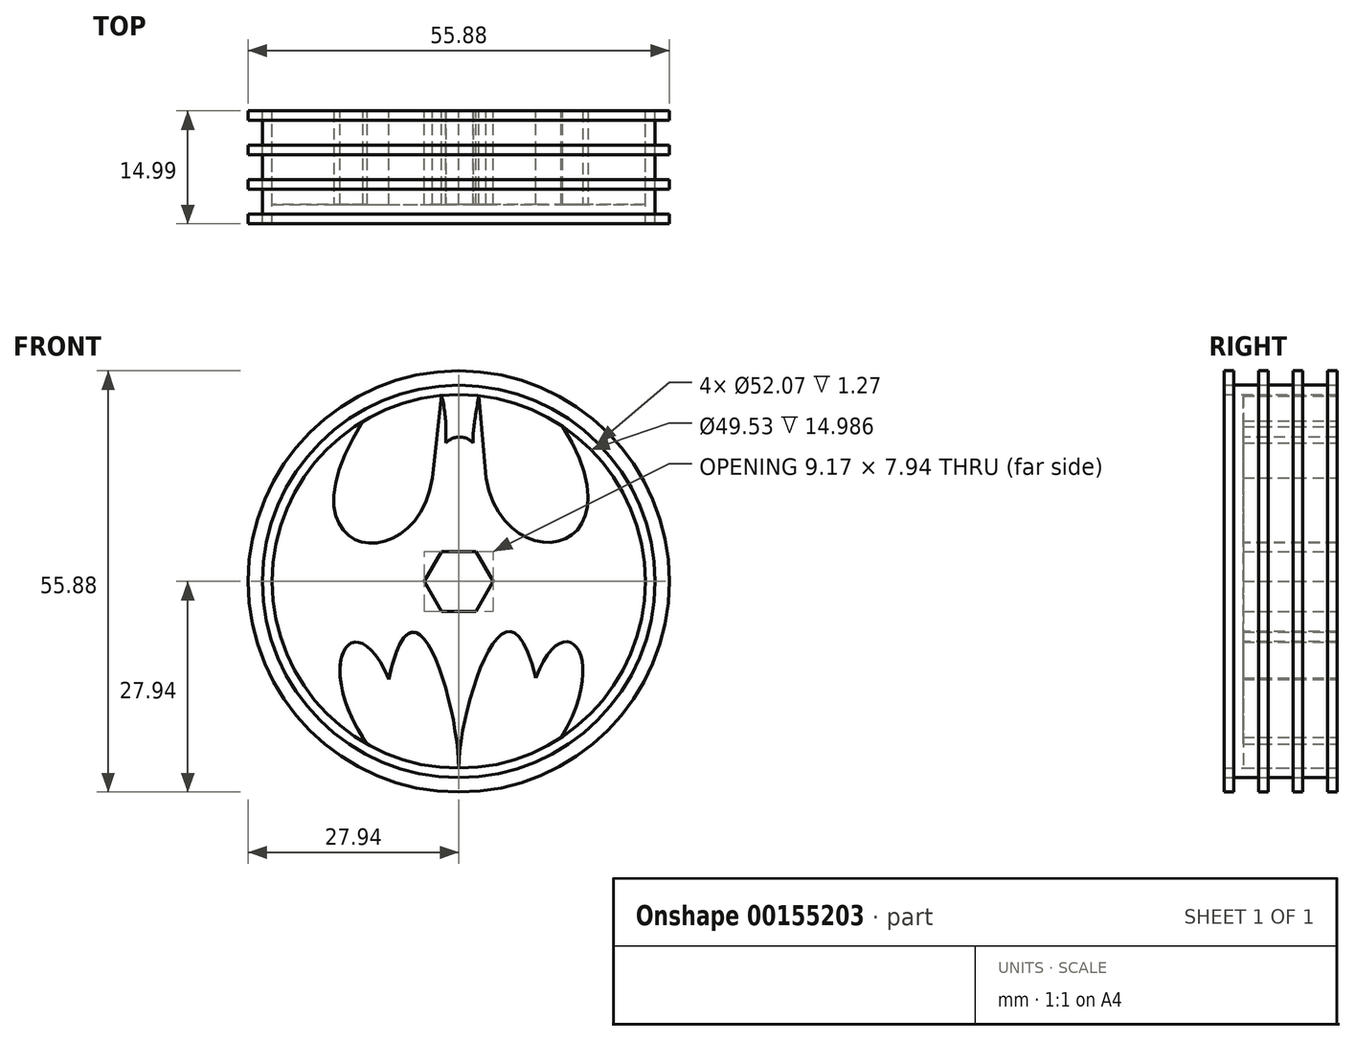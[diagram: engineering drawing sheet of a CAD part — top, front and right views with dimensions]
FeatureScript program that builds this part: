
annotation { "Feature Type Name" : "Feature", "Feature Type Description" : "" }
export const myFeature = defineFeature(function(context is Context, id is Id, definition is map)
    precondition{}
    {
        {
            var Q0;
            Q0=qCreatedBy(makeId("Front.planeOp"),FACE);
            var sketch = newSketch(context, id + "F0", { "sketchPlane" : qUnion([Q0])});
            skCircle(sketch, "E0", {"center": v(0, 0) * mm, "radius": 24.77 * mm});
            skCircle(sketch, "E1.0", {"center": v(0, 0) * mm, "radius": 27.94 * mm});
            skFitSpline(sketch, "E2", {"points": [v(-12.68, 21.27) * mm, v(-3.52, 13.73) * mm], "startDerivative": vector(-35.8, -55.66) * mm, "endDerivative": vector(6.1, 41.2) * mm});
            skLineSegment(sketch, "E3", {"start": v(-3.52, 13.73) * mm, "end": v(-2.27, 24.66) * mm});
            skFitSpline(sketch, "E4", {"points": [v(-2.27, 24.66) * mm, v(-1.73, 18.4) * mm], "startDerivative": vector(1.94, -7.74) * mm, "endDerivative": vector(-0.18, -4.73) * mm});
            skFitSpline(sketch, "E5", {"points": [v(-1.73, 18.4) * mm, v(1.9, 18.4) * mm], "startDerivative": vector(3.5, 3.03) * mm, "endDerivative": vector(3.34, -3.03) * mm});
            skFitSpline(sketch, "E6", {"points": [v(1.9, 18.4) * mm, v(2.66, 24.62) * mm], "startDerivative": vector(-0.35, 4.56) * mm, "endDerivative": vector(1.12, 7.38) * mm});
            skLineSegment(sketch, "E7", {"start": v(2.66, 24.62) * mm, "end": v(3.6, 13.73) * mm});
            skFitSpline(sketch, "E8", {"points": [v(3.6, 13.73) * mm, v(13.8, 20.56) * mm], "startDerivative": vector(7.62, -41.2) * mm, "endDerivative": vector(-32.27, 52.1) * mm});
            skFitSpline(sketch, "E9", {"points": [v(-12.16, -21.58) * mm, v(-9.28, -13) * mm], "startDerivative": vector(-22.93, 33.63) * mm, "endDerivative": vector(12.83, -31.65) * mm});
            skFitSpline(sketch, "E10", {"points": [v(-9.28, -13) * mm, v(0, -24.77) * mm], "startDerivative": vector(10.7, 49.6) * mm, "endDerivative": vector(0, -23.3) * mm});
            skFitSpline(sketch, "E11", {"points": [v(13.6, -20.7) * mm, v(10.2, -12.8) * mm], "startDerivative": vector(19.6, 32.49) * mm, "endDerivative": vector(-11.43, -30.1) * mm});
            skFitSpline(sketch, "E12", {"points": [v(10.2, -12.8) * mm, v(0, -24.77) * mm], "startDerivative": vector(-11.43, 49.15) * mm, "endDerivative": vector(0, -23.3) * mm});
            skCircle(sketch, "E13.0", {"center": v(0, 0) * mm, "radius": 26.04 * mm});
            skCircle(sketch, "E14.cCircle", {"center": v(0, 0) * mm, "radius": 4.58 * mm, "construction": true});
            skLineSegment(sketch, "E14.0", {"start": v(2.3, -3.97) * mm, "end": v(-2.3, -3.97) * mm});
            skLineSegment(sketch, "E14.1", {"start": v(-2.3, -3.97) * mm, "end": v(-4.58, 0) * mm});
            skLineSegment(sketch, "E14.2", {"start": v(-4.58, 0) * mm, "end": v(-2.3, 3.97) * mm});
            skLineSegment(sketch, "E14.3", {"start": v(-2.3, 3.97) * mm, "end": v(2.3, 3.97) * mm});
            skLineSegment(sketch, "E14.4", {"start": v(2.3, 3.97) * mm, "end": v(4.58, 0) * mm});
            skLineSegment(sketch, "E14.5", {"start": v(4.58, 0) * mm, "end": v(2.3, -3.97) * mm});
            skSolve(sketch);
        }
        {
            var Q0;
            {var subQ1=sQuery(id+"F0.wireOp",EDGE,"E2");Q0=makeQuery(id+"F0.imprint","IMPRINT",FACE,{"disambiguationData":[TD([[makeQuery(id+"F0.imprint","IMPRINT",EDGE,{"derivedFrom":subQ1}),-1.0]])]});}
            extrude(context, id + "F1", {"entities" : qUnion([Q0]), "depth" : 12.45 * mm});
        }
        {
            var Q0;
            Q0=makeQuery(id+"F0.imprint","IMPRINT",FACE,{"disambiguationData":[TD([[makeQuery(id+"F0.imprint","IMPRINT",EDGE,{"derivedFrom":sQuery(id+"F0.wireOp",EDGE,"E1.0")}),1.0]])]});
            extrude(context, id + "F2", {"entities" : qUnion([Q0]), "operationType" : NewBodyOperationType.ADD, "depth" : 1.27 * mm});
        }
        {
            var Q0;
            Q0=makeQuery(id+"F0.imprint","IMPRINT",FACE,{"disambiguationData":[TD([[makeQuery(id+"F0.imprint","IMPRINT",EDGE,{"derivedFrom":sQuery(id+"F0.wireOp",EDGE,"E1.0")}),1.0]])]});
            extrude(context, id + "F3", {"entities" : qUnion([Q0]), "operationType" : NewBodyOperationType.ADD, "depth" : 5.84 * mm, "hasSecondDirection" : true, "secondDirectionOppositeDirection" : false, "secondDirectionDepth" : 4.57 * mm});
        }
        {
            var Q0;
            Q0=makeQuery(id+"F0.imprint","IMPRINT",FACE,{"disambiguationData":[TD([[makeQuery(id+"F0.imprint","IMPRINT",EDGE,{"derivedFrom":sQuery(id+"F0.wireOp",EDGE,"E13.0")}),1.0]])]});
            extrude(context, id + "F4", {"entities" : qUnion([Q0]), "depth" : 15 * mm});
        }
        {
            var Q0;
            Q0=makeQuery(id+"F3.opExtrude","CAP_FACE",FACE,{"disambiguationData":[OSD([sQuery(id+"F0.wireOp",EDGE,"E1.0"),sQuery(id+"F0.wireOp",EDGE,"E13.0")])],"isStart":false});
            extrude(context, id + "F5", {"entities" : qUnion([Q0]), "depth" : 4.57 * mm, "hasSecondDirection" : true, "secondDirectionOppositeDirection" : false, "secondDirectionDepth" : 3.3 * mm});
        }
        {
            var Q0;
            Q0=makeQuery(id+"F5.opExtrude","CAP_FACE",FACE,{"disambiguationData":[OSD([sQuery(id+"F0.wireOp",EDGE,"E1.0"),sQuery(id+"F0.wireOp",EDGE,"E13.0")])],"isStart":false});
            extrude(context, id + "F6", {"entities" : qUnion([Q0]), "depth" : 4.57 * mm, "hasSecondDirection" : true, "secondDirectionOppositeDirection" : false, "secondDirectionDepth" : 3.3 * mm});
        }
    });
